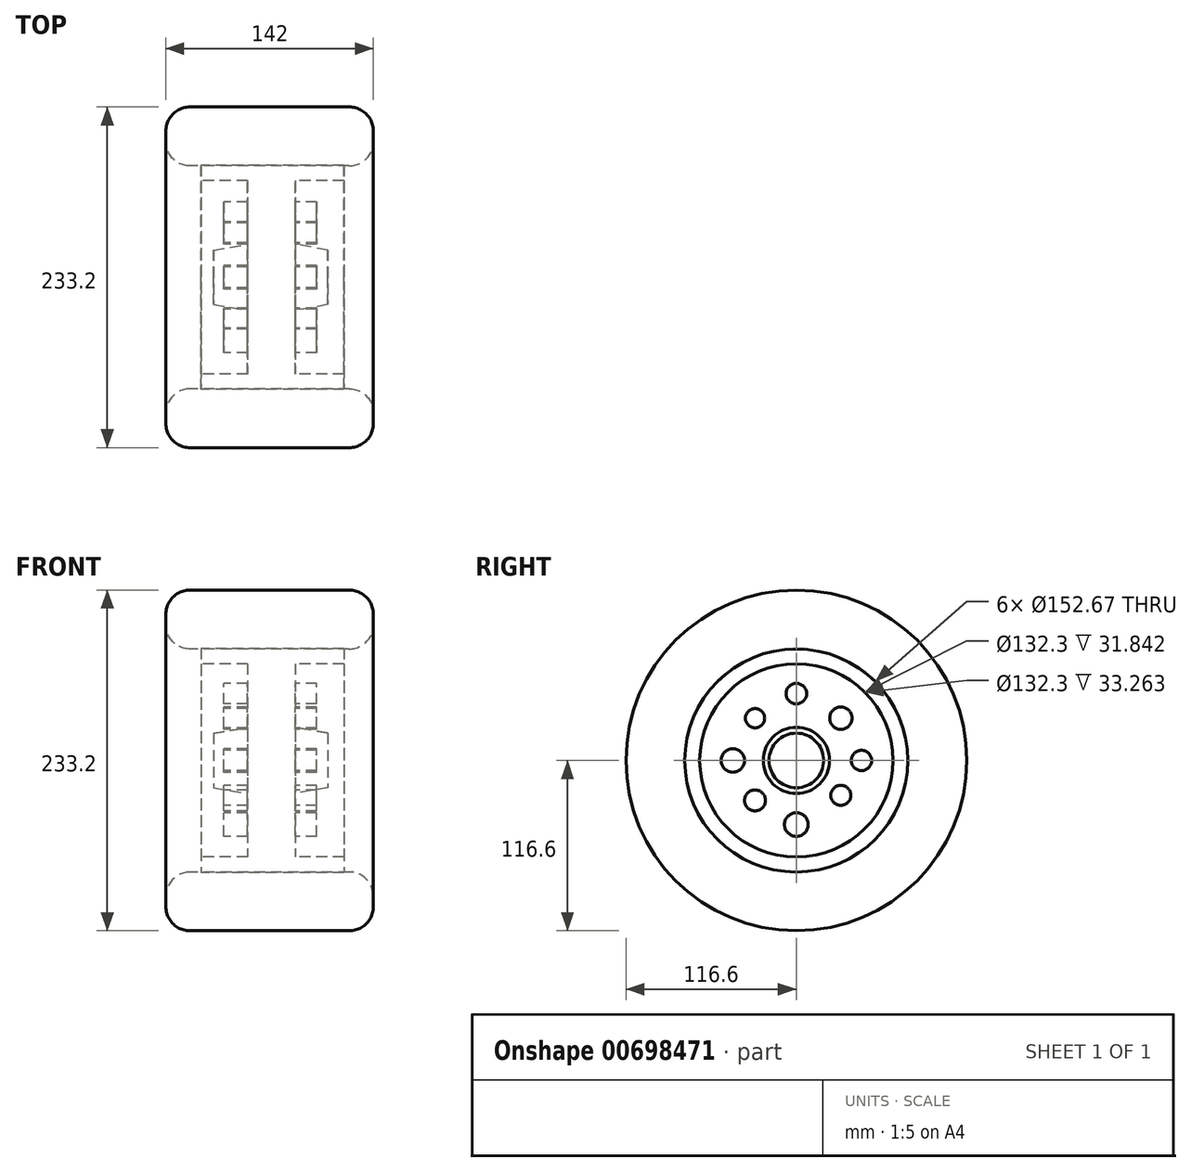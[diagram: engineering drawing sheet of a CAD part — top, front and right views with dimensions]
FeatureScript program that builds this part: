
annotation { "Feature Type Name" : "Feature", "Feature Type Description" : "" }
export const myFeature = defineFeature(function(context is Context, id is Id, definition is map)
    precondition{}
    {
        {
            var Q0;
            Q0=qCreatedBy(makeId("Front.planeOp"),FACE);
            var sketch = newSketch(context, id + "F0", { "sketchPlane" : qUnion([Q0])});
            skLineSegment(sketch, "E0.bottom", {"start": v(-47.39, 76.67) * mm, "end": v(50.41, 76.67) * mm});
            skLineSegment(sketch, "E0.top", {"start": v(-47.39, 66.15) * mm, "end": v(50.41, 66.15) * mm});
            skLineSegment(sketch, "E0.left", {"start": v(-47.39, 76.67) * mm, "end": v(-47.39, 66.15) * mm});
            skLineSegment(sketch, "E0.right", {"start": v(50.41, 76.67) * mm, "end": v(50.41, 66.15) * mm});
            skLineSegment(sketch, "E1.bottom", {"start": v(-15.55, 66.15) * mm, "end": v(17.15, 66.15) * mm});
            skLineSegment(sketch, "E1.top", {"start": v(-15.55, 22.65) * mm, "end": v(17.15, 22.65) * mm});
            skLineSegment(sketch, "E1.left", {"start": v(-15.55, 66.15) * mm, "end": v(-15.55, 22.65) * mm});
            skLineSegment(sketch, "E1.right", {"start": v(17.15, 66.15) * mm, "end": v(17.15, 22.65) * mm});
            skLineSegment(sketch, "E2", {"start": v(-15.55, 22.65) * mm, "end": v(-38.86, 18.67) * mm});
            skLineSegment(sketch, "E3", {"start": v(-38.86, 18.67) * mm, "end": v(-38.86, 0) * mm});
            skLineSegment(sketch, "E4", {"start": v(-38.86, 0) * mm, "end": v(39.32, 0) * mm});
            skLineSegment(sketch, "E5", {"start": v(39.32, 0) * mm, "end": v(39.32, 18.67) * mm});
            skLineSegment(sketch, "E6", {"start": v(39.32, 18.67) * mm, "end": v(17.15, 22.65) * mm});
            skSolve(sketch);
        }
        {
            var Q0;
            Q0 = qSketchRegion(id + "F0", true);
            var Q1;
            Q1=sQuery(id+"F0.wireOp",EDGE,"E4");
            revolve(context, id + "F1", {"entities" : qUnion([Q0]), "axis" : qUnion([Q1]), "revolveType" : RevolveType.FULL});
        }
        {
            var Q0;
            Q0=qCreatedBy(makeId("Front.planeOp"),FACE);
            var sketch = newSketch(context, id + "F2", { "sketchPlane" : qUnion([Q0])});
            skLineSegment(sketch, "E7.bottom", {"start": v(-71.46, 116.6) * mm, "end": v(70.54, 116.6) * mm});
            skLineSegment(sketch, "E7.top", {"start": v(-71.46, 76.34) * mm, "end": v(70.54, 76.34) * mm});
            skLineSegment(sketch, "E7.left", {"start": v(-71.46, 116.6) * mm, "end": v(-71.46, 76.34) * mm});
            skLineSegment(sketch, "E7.right", {"start": v(70.54, 116.6) * mm, "end": v(70.54, 76.34) * mm});
            skLineSegment(sketch, "E8", {"start": v(-75.93, 0) * mm, "end": v(87.2, 0) * mm});
            skSolve(sketch);
        }
        {
            var Q0;
            Q0 = qSketchRegion(id + "F2", true);
            var Q1;
            Q1=sQuery(id+"F2.wireOp",EDGE,"E8");
            revolve(context, id + "F3", {"entities" : qUnion([Q0]), "axis" : qUnion([Q1]), "revolveType" : RevolveType.FULL});
        }
        {
            var Q0;
            Q0=makeQuery(id+"F3.opRevolve","SWEPT_EDGE",EDGE,{"disambiguationData":[OSD([sQuery(id+"F2.wireOp",EDGE,"E7.bottom"),sQuery(id+"F2.wireOp",EDGE,"E7.left")])]});
            var Q1;
            Q1=makeQuery(id+"F3.opRevolve","SWEPT_EDGE",EDGE,{"disambiguationData":[OSD([sQuery(id+"F2.wireOp",EDGE,"E7.top"),sQuery(id+"F2.wireOp",EDGE,"E7.left")])]});
            var Q2;
            Q2=makeQuery(id+"F3.opRevolve","SWEPT_EDGE",EDGE,{"disambiguationData":[OSD([sQuery(id+"F2.wireOp",EDGE,"E7.bottom"),sQuery(id+"F2.wireOp",EDGE,"E7.right")])]});
            var Q3;
            Q3=makeQuery(id+"F3.opRevolve","SWEPT_EDGE",EDGE,{"disambiguationData":[OSD([sQuery(id+"F2.wireOp",EDGE,"E7.top"),sQuery(id+"F2.wireOp",EDGE,"E7.right")])]});
            fillet(context, id + "F4", {"entities" : qUnion([Q0, Q1, Q2, Q3]), "radius" : 16.56 * mm, "tangentPropagation" : true, "allowEdgeOverflow" : false});
        }
        {
            var Q0;
            Q0=qCreatedBy(makeId("Right.planeOp"),FACE);
            var sketch = newSketch(context, id + "F5", { "sketchPlane" : qUnion([Q0])});
            skCircle(sketch, "E9", {"center": v(-43.48, 0) * mm, "radius": 8.05 * mm});
            skCircle(sketch, "E10", {"center": v(0, 45.74) * mm, "radius": 7.04 * mm});
            skCircle(sketch, "E11", {"center": v(44.54, 0) * mm, "radius": 6.96 * mm});
            skCircle(sketch, "E12", {"center": v(0, -43.88) * mm, "radius": 8.11 * mm});
            skCircle(sketch, "E13", {"center": v(-28.27, 28.94) * mm, "radius": 6.59 * mm});
            skCircle(sketch, "E14", {"center": v(30.4, 28.94) * mm, "radius": 7.64 * mm});
            skCircle(sketch, "E15", {"center": v(30.4, -23.87) * mm, "radius": 6.86 * mm});
            skCircle(sketch, "E16", {"center": v(-28.27, -27.34) * mm, "radius": 7.16 * mm});
            skSolve(sketch);
        }
        {
            var Q0;
            Q0 = qSketchRegion(id + "F5", true);
            extrude(context, id + "F6", {"entities" : qUnion([Q0]), "operationType" : NewBodyOperationType.ADD, "endBound" : BoundingType.SYMMETRIC, "depth" : 63.5 * mm, "offsetDistance" : 25.4 * mm});
        }
    });
